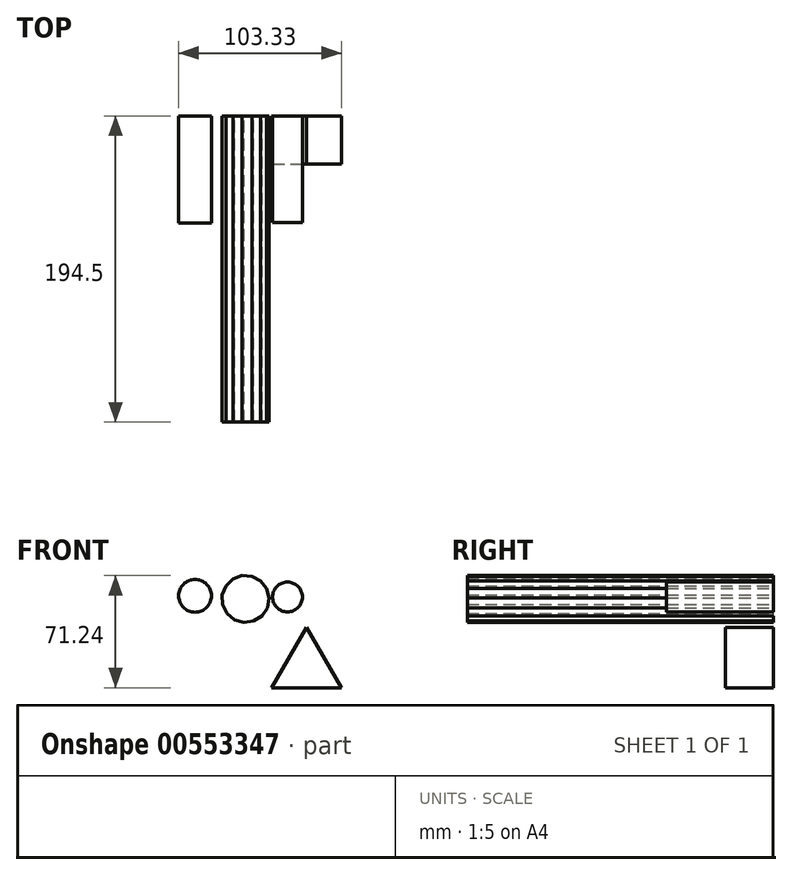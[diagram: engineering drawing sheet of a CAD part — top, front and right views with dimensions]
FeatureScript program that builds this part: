
annotation { "Feature Type Name" : "Feature", "Feature Type Description" : "" }
export const myFeature = defineFeature(function(context is Context, id is Id, definition is map)
    precondition{}
    {
        {
            var Q0;
            Q0=qCreatedBy(makeId("Front.planeOp"),FACE);
            var sketch = newSketch(context, id + "F0", { "sketchPlane" : qUnion([Q0])});
            skLineSegment(sketch, "E0", {"start": v(-22.1, -13.03) * mm, "end": v(22.1, -13.03) * mm});
            skLineSegment(sketch, "E1", {"start": v(-22.1, -13.03) * mm, "end": v(0, 25.24) * mm});
            skLineSegment(sketch, "E2", {"start": v(22.1, -13.03) * mm, "end": v(0, 25.24) * mm});
            skSolve(sketch);
        }
        {
            var Q0;
            Q0 = qSketchRegion(id + "F0", true);
            extrude(context, id + "F1", {"entities" : qUnion([Q0]), "depth" : 30.6 * mm, "offsetDistance" : 25 * mm});
        }
        {
            var Q0;
            Q0=qCreatedBy(makeId("Front.planeOp"),FACE);
            var sketch = newSketch(context, id + "F2", { "sketchPlane" : qUnion([Q0])});
            skCircle(sketch, "E3.cCircle", {"center": v(-38.8, 43.34) * mm, "radius": 14.7 * mm, "construction": true});
            skLineSegment(sketch, "E3.0", {"start": v(-24.88, 37.71) * mm, "end": v(-28.37, 32.54) * mm});
            skLineSegment(sketch, "E3.1", {"start": v(-28.37, 32.54) * mm, "end": v(-33.67, 29.23) * mm});
            skLineSegment(sketch, "E3.2", {"start": v(-33.67, 29.23) * mm, "end": v(-39.86, 28.36) * mm});
            skLineSegment(sketch, "E3.3", {"start": v(-39.86, 28.36) * mm, "end": v(-45.86, 30.08) * mm});
            skLineSegment(sketch, "E3.4", {"start": v(-45.86, 30.08) * mm, "end": v(-50.64, 34.1) * mm});
            skLineSegment(sketch, "E3.5", {"start": v(-50.64, 34.1) * mm, "end": v(-53.38, 39.7) * mm});
            skLineSegment(sketch, "E3.6", {"start": v(-53.38, 39.7) * mm, "end": v(-53.6, 45.95) * mm});
            skLineSegment(sketch, "E3.7", {"start": v(-53.6, 45.95) * mm, "end": v(-51.26, 51.74) * mm});
            skLineSegment(sketch, "E3.8", {"start": v(-51.26, 51.74) * mm, "end": v(-46.77, 56.08) * mm});
            skLineSegment(sketch, "E3.9", {"start": v(-46.77, 56.08) * mm, "end": v(-40.9, 58.21) * mm});
            skLineSegment(sketch, "E3.10", {"start": v(-40.9, 58.21) * mm, "end": v(-34.67, 57.78) * mm});
            skLineSegment(sketch, "E3.11", {"start": v(-34.67, 57.78) * mm, "end": v(-29.15, 54.85) * mm});
            skLineSegment(sketch, "E3.12", {"start": v(-29.15, 54.85) * mm, "end": v(-25.3, 49.93) * mm});
            skLineSegment(sketch, "E3.13", {"start": v(-25.3, 49.93) * mm, "end": v(-23.8, 43.87) * mm});
            skLineSegment(sketch, "E3.14", {"start": v(-23.8, 43.87) * mm, "end": v(-24.88, 37.71) * mm});
            skPoint(sketch, "E3.0.midPoint", {"position": v(-26.63, 35.13) * mm});
            skSolve(sketch);
        }
        {
            var Q0;
            Q0 = qSketchRegion(id + "F2", true);
            extrude(context, id + "F3", {"entities" : qUnion([Q0]), "depth" : 194.5 * mm, "offsetDistance" : 25 * mm});
        }
        {
            var Q0;
            Q0=qCreatedBy(makeId("Front.planeOp"),FACE);
            var sketch = newSketch(context, id + "F4", { "sketchPlane" : qUnion([Q0])});
            skCircle(sketch, "E4", {"center": v(-70.82, 45.32) * mm, "radius": 10.42 * mm});
            skSolve(sketch);
        }
        {
            var Q0;
            Q0 = qSketchRegion(id + "F4", true);
            extrude(context, id + "F5", {"entities" : qUnion([Q0]), "depth" : 68.1 * mm, "offsetDistance" : 25 * mm});
        }
        {
            var Q0;
            Q0=qCreatedBy(makeId("Front.planeOp"),FACE);
            var sketch = newSketch(context, id + "F6", { "sketchPlane" : qUnion([Q0])});
            skCircle(sketch, "E5", {"center": v(-12.15, 44.56) * mm, "radius": 9.48 * mm});
            skSolve(sketch);
        }
        {
            var Q0;
            Q0 = qSketchRegion(id + "F6", true);
            extrude(context, id + "F7", {"entities" : qUnion([Q0]), "depth" : 67.9 * mm, "offsetDistance" : 25 * mm});
        }
    });
